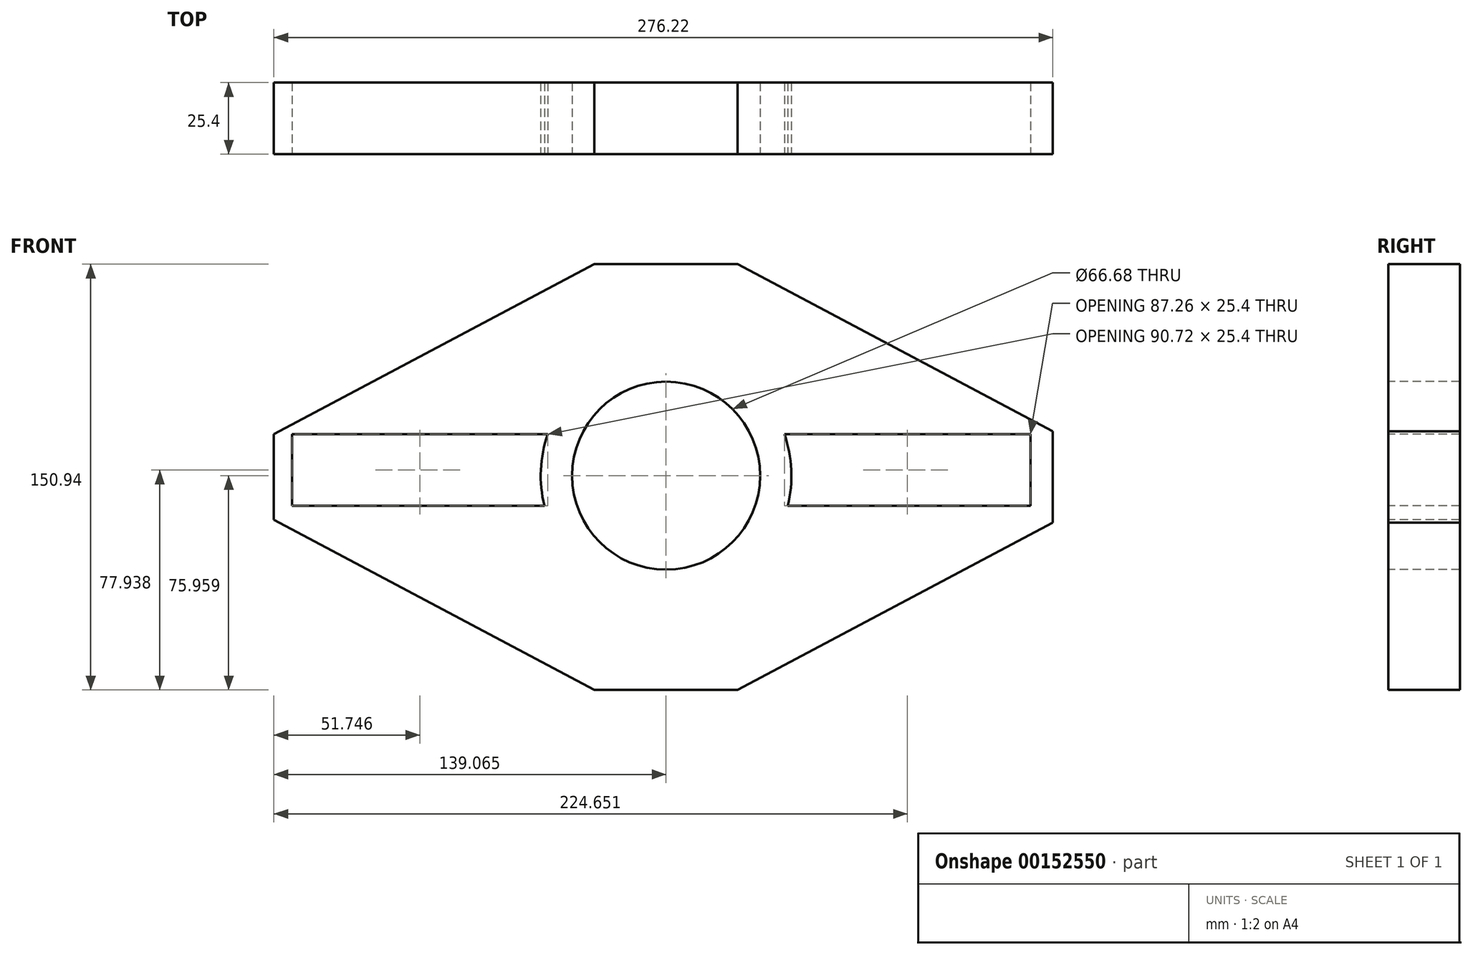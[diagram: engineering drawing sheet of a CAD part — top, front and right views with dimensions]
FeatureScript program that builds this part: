
annotation { "Feature Type Name" : "Feature", "Feature Type Description" : "" }
export const myFeature = defineFeature(function(context is Context, id is Id, definition is map)
    precondition{}
    {
        {
            var Q0;
            Q0=qCreatedBy(makeId("Front.planeOp"),FACE);
            var sketch = newSketch(context, id + "F0", { "sketchPlane" : qUnion([Q0])});
            skLineSegment(sketch, "E0.bottom", {"start": v(138.11, 75.47) * mm, "end": v(-138.11, 75.47) * mm});
            skLineSegment(sketch, "E0.top", {"start": v(138.11, -75.47) * mm, "end": v(-138.11, -75.47) * mm});
            skLineSegment(sketch, "E0.left", {"start": v(138.11, 75.47) * mm, "end": v(138.11, -75.47) * mm});
            skLineSegment(sketch, "E0.right", {"start": v(-138.11, 75.47) * mm, "end": v(-138.11, -75.47) * mm});
            skPoint(sketch, "E0.middle", {"position": v(0, 0) * mm});
            skSolve(sketch);
        }
        {
            var Q0;
            Q0 = qSketchRegion(id + "F0", true);
            extrude(context, id + "F1", {"entities" : qUnion([Q0]), "depth" : 25.4 * mm});
        }
        {
            var Q0;
            Q0=makeQuery(id+"F1.opExtrude","CAP_FACE",FACE,{"disambiguationData":[OSD([sQuery(id+"F0.wireOp",EDGE,"E0.bottom"),sQuery(id+"F0.wireOp",EDGE,"E0.top"),sQuery(id+"F0.wireOp",EDGE,"E0.left"),sQuery(id+"F0.wireOp",EDGE,"E0.right")])],"isStart":false});
            var sketch = newSketch(context, id + "F2", { "sketchPlane" : qUnion([Q0])});
            skPoint(sketch, "E1.orphan", {"position": v(0.95, 69.88) * mm});
            skPoint(sketch, "E2.start.orphan", {"position": v(-145.2, 8.75) * mm});
            skPoint(sketch, "E3.centerSnap0", {"position": v(-145.2, 6.38) * mm});
            skCircle(sketch, "E4", {"center": v(0.95, 0.49) * mm, "radius": 33.34 * mm});
            skCircle(sketch, "E5", {"center": v(0.95, 0.49) * mm, "radius": 44.45 * mm});
            skLineSegment(sketch, "E6", {"start": v(138.11, 15.17) * mm, "end": v(138.11, -10.23) * mm});
            skLineSegment(sketch, "E7", {"start": v(-138.11, 15.17) * mm, "end": v(-138.11, -10.23) * mm});
            skLineSegment(sketch, "E8", {"start": v(-138.11, 15.17) * mm, "end": v(-41, 15.17) * mm});
            skLineSegment(sketch, "E9", {"start": v(-138.11, -10.23) * mm, "end": v(-42.18, -10.23) * mm});
            skLineSegment(sketch, "E10", {"start": v(138.11, 15.17) * mm, "end": v(42.91, 15.17) * mm});
            skLineSegment(sketch, "E11", {"start": v(138.11, -10.23) * mm, "end": v(44.1, -10.23) * mm});
            skLineSegment(sketch, "E12", {"start": v(0, 0) * mm, "end": v(0.95, 75.47) * mm});
            skPoint(sketch, "E12.endSnap0", {"position": v(0, 75.47) * mm});
            skLineSegment(sketch, "E13", {"start": v(0.95, 75.47) * mm, "end": v(0.95, -75.47) * mm});
            skLineSegment(sketch, "E14", {"start": v(0.95, -75.47) * mm, "end": v(138.11, -75.47) * mm});
            skLineSegment(sketch, "E15", {"start": v(138.11, -75.47) * mm, "end": v(138.11, 75.47) * mm});
            skLineSegment(sketch, "E16", {"start": v(138.11, 75.47) * mm, "end": v(0.95, 75.47) * mm});
            skLineSegment(sketch, "E17", {"start": v(-138.11, 75.47) * mm, "end": v(-138.11, -75.47) * mm});
            skLineSegment(sketch, "E18", {"start": v(-138.11, -75.47) * mm, "end": v(0.95, -75.47) * mm});
            skLineSegment(sketch, "E19", {"start": v(0.95, 75.47) * mm, "end": v(0.95, 80.4) * mm});
            skLineSegment(sketch, "E20", {"start": v(0.95, 80.4) * mm, "end": v(-24.45, 80.4) * mm});
            skLineSegment(sketch, "E21", {"start": v(0.95, 80.4) * mm, "end": v(26.38, 80.4) * mm});
            skLineSegment(sketch, "E22", {"start": v(-24.45, 80.4) * mm, "end": v(-24.45, 75.47) * mm});
            skLineSegment(sketch, "E23", {"start": v(-24.45, 75.47) * mm, "end": v(-138.11, 15.17) * mm});
            skLineSegment(sketch, "E24.MirrorCS", {"start": v(26.35, 75.47) * mm, "end": v(140.02, 15.17) * mm});
            skLineSegment(sketch, "E25.MirrorCS", {"start": v(26.35, -75.47) * mm, "end": v(140.02, -15.17) * mm});
            skLineSegment(sketch, "E26.MirrorCS", {"start": v(-24.45, -75.47) * mm, "end": v(-138.11, -15.17) * mm});
            skLineSegment(sketch, "E27", {"start": v(-131.73, 15.17) * mm, "end": v(-131.73, -10.23) * mm});
            skLineSegment(sketch, "E28", {"start": v(130.17, 15.17) * mm, "end": v(130.17, -10.23) * mm});
            skSolve(sketch);
        }
        {
            var Q0;
            {var subQ3=sQuery(id+"F2.wireOp",EDGE,"E23");Q0=makeQuery(id+"F2.imprint","IMPRINT",FACE,{"disambiguationData":[TD([[makeQuery(id+"F2.imprint","IMPRINT",EDGE,{"derivedFrom":subQ3}),-1.0]])]});}
            var Q1;
            {var subQ3=sQuery(id+"F2.wireOp",EDGE,"E26.MirrorCS");Q1=makeQuery(id+"F2.imprint","IMPRINT",FACE,{"disambiguationData":[TD([[makeQuery(id+"F2.imprint","IMPRINT",EDGE,{"derivedFrom":subQ3}),1.0]])]});}
            var Q2;
            {var subQ0=sQuery(id+"F2.wireOp",EDGE,"E16");var subQ1=sQuery(id+"F2.wireOp",EDGE,"E15");var subQ2=makeQuery(id+"F2.imprint","INTERSECT",VERTEX,{"derivedFrom":[subQ1,subQ0]});Q2=makeQuery(id+"F2.imprint","IMPRINT",FACE,{"disambiguationData":[TD([[makeQuery(id+"F2.imprint","IMPRINT",EDGE,{"disambiguationData":[TD([[subQ2,-1.0]])],"derivedFrom":subQ1}),-1.0]])]});}
            var Q3;
            {var subQ0=sQuery(id+"F2.wireOp",EDGE,"E15");var subQ1=sQuery(id+"F2.wireOp",EDGE,"E14");var subQ2=makeQuery(id+"F2.imprint","INTERSECT",VERTEX,{"derivedFrom":[subQ1,subQ0]});Q3=makeQuery(id+"F2.imprint","IMPRINT",FACE,{"disambiguationData":[TD([[makeQuery(id+"F2.imprint","IMPRINT",EDGE,{"disambiguationData":[TD([[subQ2,-1.0]])],"derivedFrom":subQ1}),-1.0]])]});}
            var Q4;
            {var subQ0=sQuery(id+"F2.wireOp",EDGE,"E4");var subQ1=makeQuery(id+"F2.imprint","INTERSECT",VERTEX,{"derivedFrom":[subQ0,sQuery(id+"F2.wireOp",EDGE,"E12")]});Q4=makeQuery(id+"F2.imprint","IMPRINT",FACE,{"disambiguationData":[TD([[makeQuery(id+"F2.imprint","IMPRINT",EDGE,{"disambiguationData":[TD([[subQ1,1.0]])],"derivedFrom":subQ0}),1.0]])]});}
            var Q5;
            {var subQ0=sQuery(id+"F2.wireOp",EDGE,"E13");var subQ1=sQuery(id+"F2.wireOp",EDGE,"E4");var subQ2=makeQuery(id+"F2.imprint","INTERSECT",VERTEX,{"disambiguationData":[OD(0.0)],"derivedFrom":[subQ1,subQ0]});Q5=makeQuery(id+"F2.imprint","IMPRINT",FACE,{"disambiguationData":[TD([[makeQuery(id+"F2.imprint","IMPRINT",EDGE,{"disambiguationData":[TD([[subQ2,1.0]])],"derivedFrom":subQ1}),1.0]])]});}
            var Q6;
            {var subQ5=sQuery(id+"F2.wireOp",EDGE,"E27");Q6=makeQuery(id+"F2.imprint","IMPRINT",FACE,{"disambiguationData":[TD([[makeQuery(id+"F2.imprint","IMPRINT",EDGE,{"derivedFrom":subQ5}),1.0]])]});}
            var Q7;
            {var subQ5=sQuery(id+"F2.wireOp",EDGE,"E28");Q7=makeQuery(id+"F2.imprint","IMPRINT",FACE,{"disambiguationData":[TD([[makeQuery(id+"F2.imprint","IMPRINT",EDGE,{"derivedFrom":subQ5}),-1.0]])]});}
            extrude(context, id + "F3", {"entities" : qUnion([Q0, Q1, Q2, Q3, Q4, Q5, Q6, Q7]), "operationType" : NewBodyOperationType.REMOVE, "oppositeDirection" : true, "depth" : 25.4 * mm});
        }
    });
